# Revit family: Kombiventil F_4006
name_source: partatom
category: Rohrzubehör
units: mm (PartAtom-declared; Revit-internal decimal feet)

## family parameters
Arbeitsebenenbasiert = Nein
Beim Laden mit Abzugskörper schneiden = Nein
Bemaßung runder Anschluss = Durchmesser verwenden
Gemeinsam genutzt = Nein
Immer vertikal = Ja
OmniClass-Nummer = 23.65.55.14
OmniClass-Titel = Valves for Liquid Services
Teiletyp = Unterbricht

## types (1)
- Kombiventil F_4006
    Anschlussflansch = EN 1092-2
    Anwendungsgebiet = Das Kombiventil wird in allen pumpenbetriebenen Heiz- und Kühlanlagen eingesetzt. Der Regler begrenzt automatisch den Volumenstrom im gewählten Anlagenteil auf den einmal eingestellten Wert, indem alle Druckschwankungen gemessen und ausgeregelt werden. Somit sind keine Messungen erforderlich und die Regelung ist bei allen Betriebsbedingungen effektiv. Das Kombiventil regelt den Volumenstrom der ventileigenen Voreinstellung auf einen
konstanten Wert; die Membran regelt aufgrund des Druckes unmittelbar nach dem Regeleinsatz, sowie des Druckes davor.
    D03 = 21 mm  [stored 0.0688976 ft]
    D07 = 30 mm  [stored 0.0984252 ft]
    D08 = 24 mm  [stored 0.0787402 ft]
    D13 = 16 mm  [stored 0.0524934 ft]
    D14 = 17 mm  [stored 0.0557743 ft]
    D15 = 5 mm  [stored 0.0164042 ft]
    D16 = 10 mm  [stored 0.0328084 ft]
    D17 = 3 mm  [stored 0.00984252 ft]
    D18 = 4 mm  [stored 0.0131234 ft]
    Dichtungen = EPDM
    Differenzdruck ü. Mengenbegrenzer = 20000.0 Pa
    Gehäuse = EN-GJL-250
    H04 = 5 mm  [stored 0.0164042 ft]
    H05 = 3 mm  [stored 0.00984252 ft]
    H08 = 21 mm  [stored 0.0688976 ft]
    H16 = 3 mm  [stored 0.00984252 ft]
    H17 = 5 mm  [stored 0.0164042 ft]
    H18 = 4 mm  [stored 0.0131234 ft]
    Hersteller = HERZ Armaturen Ges.m.b.H.
    Impulsleitung = WN1.4301
    K00 = 24 mm  [stored 0.0787402 ft]
    K01 = 4 mm  [stored 0.0131234 ft]
    K02 = 5 mm  [stored 0.0164042 ft]
    K03 = 14 mm  [stored 0.0459318 ft]
    Kegel = CW617N-R320-S
    L01 = 3 mm  [stored 0.00984252 ft]
    L03 = 10 mm  [stored 0.0328084 ft]
    M00 = 27 mm  [stored 0.0885827 ft]
    M01 = 9 mm  [stored 0.0295276 ft]
    M02 = 6 mm  [stored 0.019685 ft]
    M03 = 3 mm  [stored 0.00984252 ft]
    M04 = 2 mm  [stored 0.00656168 ft]
    M05 = 4 mm  [stored 0.0131234 ft]
    Max. Betriebsdruck = 1600000.0 Pa
    Max. Betriebstemperatur = 110 °C
    Medium = Heizungswasserqualität nach ÖNORM H 5195 oder VDI-Richtline 2035.
Die Verwendung von Ethylen- oder
Propylenglykol in einem Mischungsverhältnis 25 - 50% ist zulässig.
    Membrane = EPDM
    Min. Betriebdruck = 400000.0 Pa
    Min. Betriebstemperatur (Frostschutz) = -20 °C
    Min. Betriebstemperatur (reines Wasser) = 2 °C
    R02 = 13 mm
    R03 = 7 mm  [stored 0.0229659 ft]
    R04 = 8 mm  [stored 0.0262467 ft]
    R05 = 5 mm  [stored 0.0164042 ft]
    R97 = 2 mm  [stored 0.00656168 ft]
    R98 = 6 mm  [stored 0.019685 ft]
    R99 = 14 mm  [stored 0.0459318 ft]
    SCRNCODE = 05;04;02
    SCRNSEQ = ARM;ARM_TYP="DURR";2
    Sitz = WN1.4305
    Spindel = WN1.4305
    URL = www.herz-armaturen.at
    Vorgabe-Ansicht = 0 mm  [stored 0 ft]

note: [stored X ft] marks values corroborated as IEEE doubles in the binary element streams (Revit-internal decimal feet)
